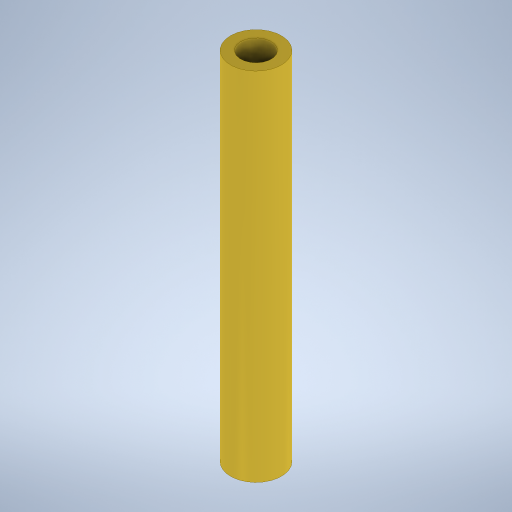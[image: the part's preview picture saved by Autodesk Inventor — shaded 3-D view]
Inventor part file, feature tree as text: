
AUTODESK INVENTOR PART (.ipt)
format: ipt  version: 2023 (Build 270158000, 158)  size: 227,840 bytes
history: native  units: in
note: dims shown in document units (in); Inventor stores cm internally (conversion verified against a paired STEP export)
features: extrude x1, sketch x1
ambient origin geometry x8: Origin, YZ Plane, XZ Plane, XY Plane, X Axis, Y Axis, Z Axis, Center Point
bodies: Solid1 (feature_tree)
feature tree (2):
  extrude  "Extrusion1"  Depth=1.378in
  sketch  "Sketch1"  dims[d0=0.1969in d1=0.1181in d2=1.378in d3=0.0in]
